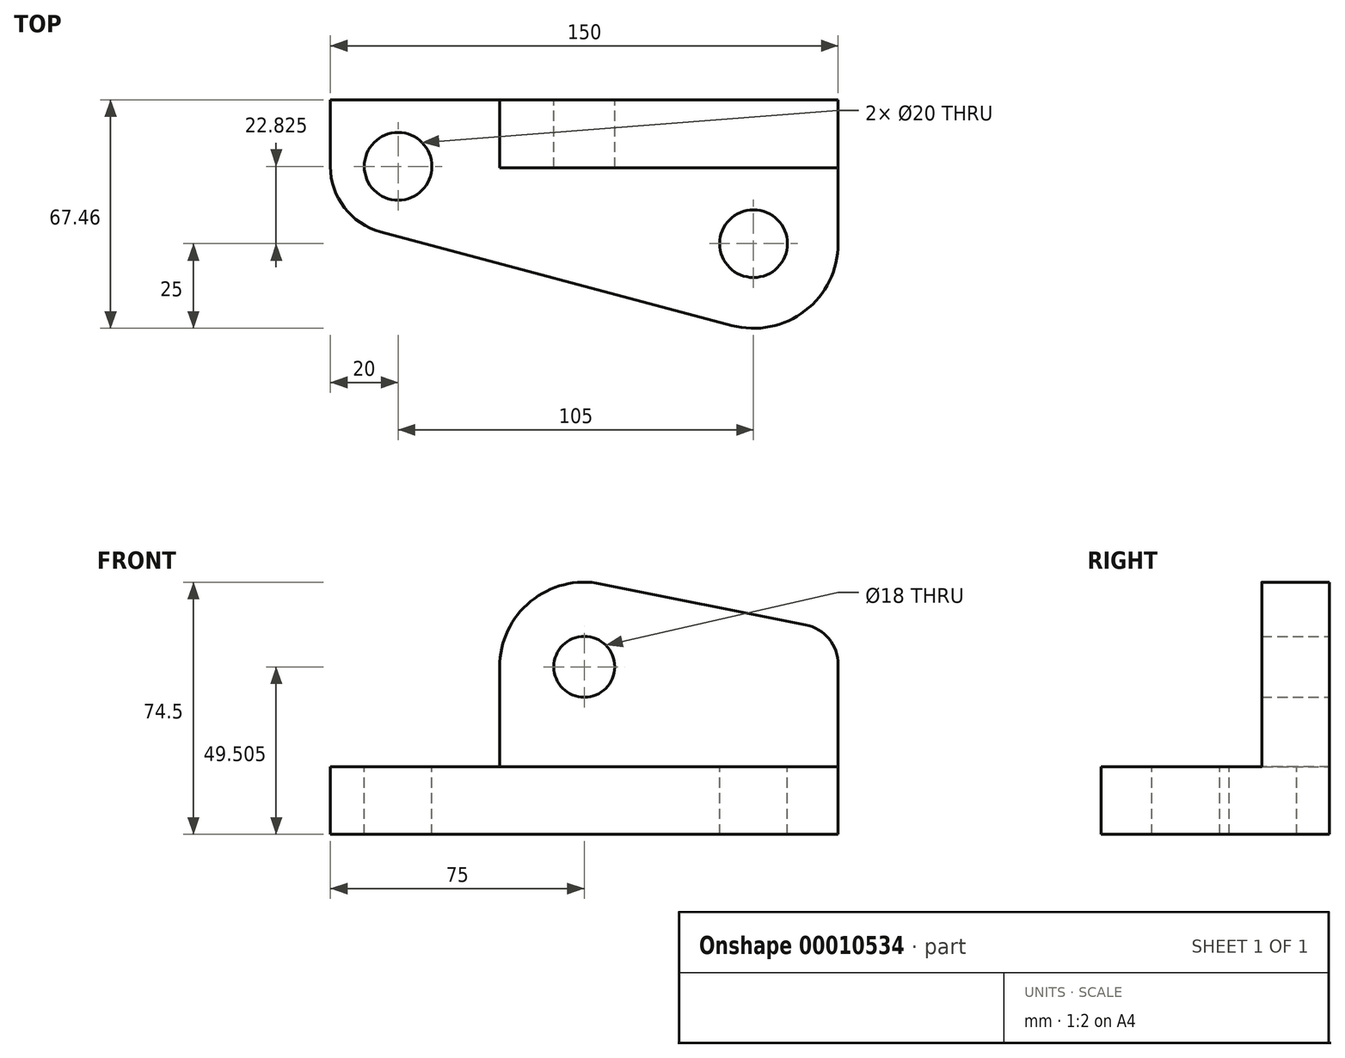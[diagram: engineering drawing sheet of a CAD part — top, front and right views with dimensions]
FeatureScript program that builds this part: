
annotation { "Feature Type Name" : "Feature", "Feature Type Description" : "" }
export const myFeature = defineFeature(function(context is Context, id is Id, definition is map)
    precondition{}
    {
        {
            var Q0;
            Q0=qCreatedBy(makeId("Top.planeOp"),FACE);
            var sketch = newSketch(context, id + "F0", { "sketchPlane" : qUnion([Q0])});
            skLineSegment(sketch, "E0", {"start": v(0, 0) * mm, "end": v(0, -35) * mm});
            skLineSegment(sketch, "E1", {"start": v(0, -35) * mm, "end": v(150, -75) * mm});
            skLineSegment(sketch, "E2", {"start": v(150, -75) * mm, "end": v(150, 0) * mm});
            skLineSegment(sketch, "E3", {"start": v(150, 0) * mm, "end": v(0, 0) * mm});
            skSolve(sketch);
        }
        {
            var Q0;
            Q0=qSketchRegion(id+"F0",true);
            extrude(context, id + "F1", {"entities" : qUnion([Q0]), "depth" : 20 * mm});
        }
        {
            var Q0;
            Q0=makeQuery(id+"F1.opExtrude","SWEPT_FACE",FACE,{"disambiguationData":[OSD([sQuery(id+"F0.wireOp",EDGE,"E3")])]});
            var sketch = newSketch(context, id + "F2", { "sketchPlane" : qUnion([Q0])});
            skLineSegment(sketch, "E4", {"start": v(-150, 0) * mm, "end": v(-150, 60) * mm});
            skLineSegment(sketch, "E5", {"start": v(-150, 60) * mm, "end": v(-50, 80) * mm});
            skLineSegment(sketch, "E6", {"start": v(-50, 80) * mm, "end": v(-50, 0) * mm});
            skLineSegment(sketch, "E7", {"start": v(-50, 0) * mm, "end": v(-150, 0) * mm});
            skSolve(sketch);
        }
        {
            var Q0;
            Q0=qSketchRegion(id+"F2",true);
            extrude(context, id + "F3", {"entities" : qUnion([Q0]), "operationType" : NewBodyOperationType.ADD, "oppositeDirection" : true, "depth" : 20 * mm});
        }
        {
            var Q0;
            Q0=makeQuery(id+"F1.opExtrude","SWEPT_EDGE",EDGE,{"disambiguationData":[OSD([sQuery(id+"F0.wireOp",EDGE,"E0"),sQuery(id+"F0.wireOp",EDGE,"E1")])]});
            fillet(context, id + "F4", {"entities" : qUnion([Q0]), "radius" : 20 * mm, "tangentPropagation" : true, "allowEdgeOverflow" : false});
        }
        {
            var Q0;
            Q0=makeQuery(id+"F1.opExtrude","SWEPT_EDGE",EDGE,{"disambiguationData":[OSD([sQuery(id+"F0.wireOp",EDGE,"E1"),sQuery(id+"F0.wireOp",EDGE,"E2")])]});
            var Q1;
            Q1=makeQuery(id+"F3.opExtrude","SWEPT_EDGE",EDGE,{"disambiguationData":[OSD([sQuery(id+"F2.wireOp",EDGE,"E5"),sQuery(id+"F2.wireOp",EDGE,"E6")])]});
            fillet(context, id + "F5", {"entities" : qUnion([Q0, Q1]), "radius" : 25 * mm, "tangentPropagation" : true, "allowEdgeOverflow" : false});
        }
        {
            var Q0;
            Q0=makeQuery(id+"F3.opExtrude","SWEPT_EDGE",EDGE,{"disambiguationData":[OSD([sQuery(id+"F2.wireOp",EDGE,"E4"),sQuery(id+"F2.wireOp",EDGE,"E5")])]});
            fillet(context, id + "F6", {"entities" : qUnion([Q0]), "radius" : 12 * mm, "tangentPropagation" : true, "allowEdgeOverflow" : false});
        }
        {
            var Q0;
            Q0=makeQuery(id+"F1.opExtrude","CAP_FACE",FACE,{"disambiguationData":[OSD([sQuery(id+"F0.wireOp",EDGE,"E0"),sQuery(id+"F0.wireOp",EDGE,"E1"),sQuery(id+"F0.wireOp",EDGE,"E2"),sQuery(id+"F0.wireOp",EDGE,"E3")])],"isStart":false});
            var sketch = newSketch(context, id + "F7", { "sketchPlane" : qUnion([Q0])});
            skCircle(sketch, "E8", {"center": v(20, -19.63) * mm, "radius": 10 * mm});
            skCircle(sketch, "E9", {"center": v(125, -42.46) * mm, "radius": 10 * mm});
            skSolve(sketch);
        }
        {
            var Q0;
            Q0=qSketchRegion(id+"F7",true);
            extrude(context, id + "F8", {"entities" : qUnion([Q0]), "operationType" : NewBodyOperationType.REMOVE, "endBound" : BoundingType.THROUGH_ALL, "oppositeDirection" : true, "depth" : 25 * mm});
        }
        {
            var Q0;
            Q0=makeQuery(id+"F3.boolean.opBoolean","MERGE",FACE,{"derivedFrom":[makeQuery(id+"F1.opExtrude","SWEPT_FACE",FACE,{"disambiguationData":[OSD([sQuery(id+"F0.wireOp",EDGE,"E3")])]}),makeQuery(id+"F3.opExtrude","CAP_FACE",FACE,{"disambiguationData":[OSD([sQuery(id+"F2.wireOp",EDGE,"E4"),sQuery(id+"F2.wireOp",EDGE,"E5"),sQuery(id+"F2.wireOp",EDGE,"E6"),sQuery(id+"F2.wireOp",EDGE,"E7")])],"isStart":true})]});
            var sketch = newSketch(context, id + "F9", { "sketchPlane" : qUnion([Q0])});
            skCircle(sketch, "E10", {"center": v(-75, 49.5) * mm, "radius": 9 * mm});
            skSolve(sketch);
        }
        {
            var Q0;
            Q0=qSketchRegion(id+"F9",true);
            extrude(context, id + "F10", {"entities" : qUnion([Q0]), "operationType" : NewBodyOperationType.REMOVE, "endBound" : BoundingType.THROUGH_ALL, "oppositeDirection" : true, "depth" : 25 * mm});
        }
    });
